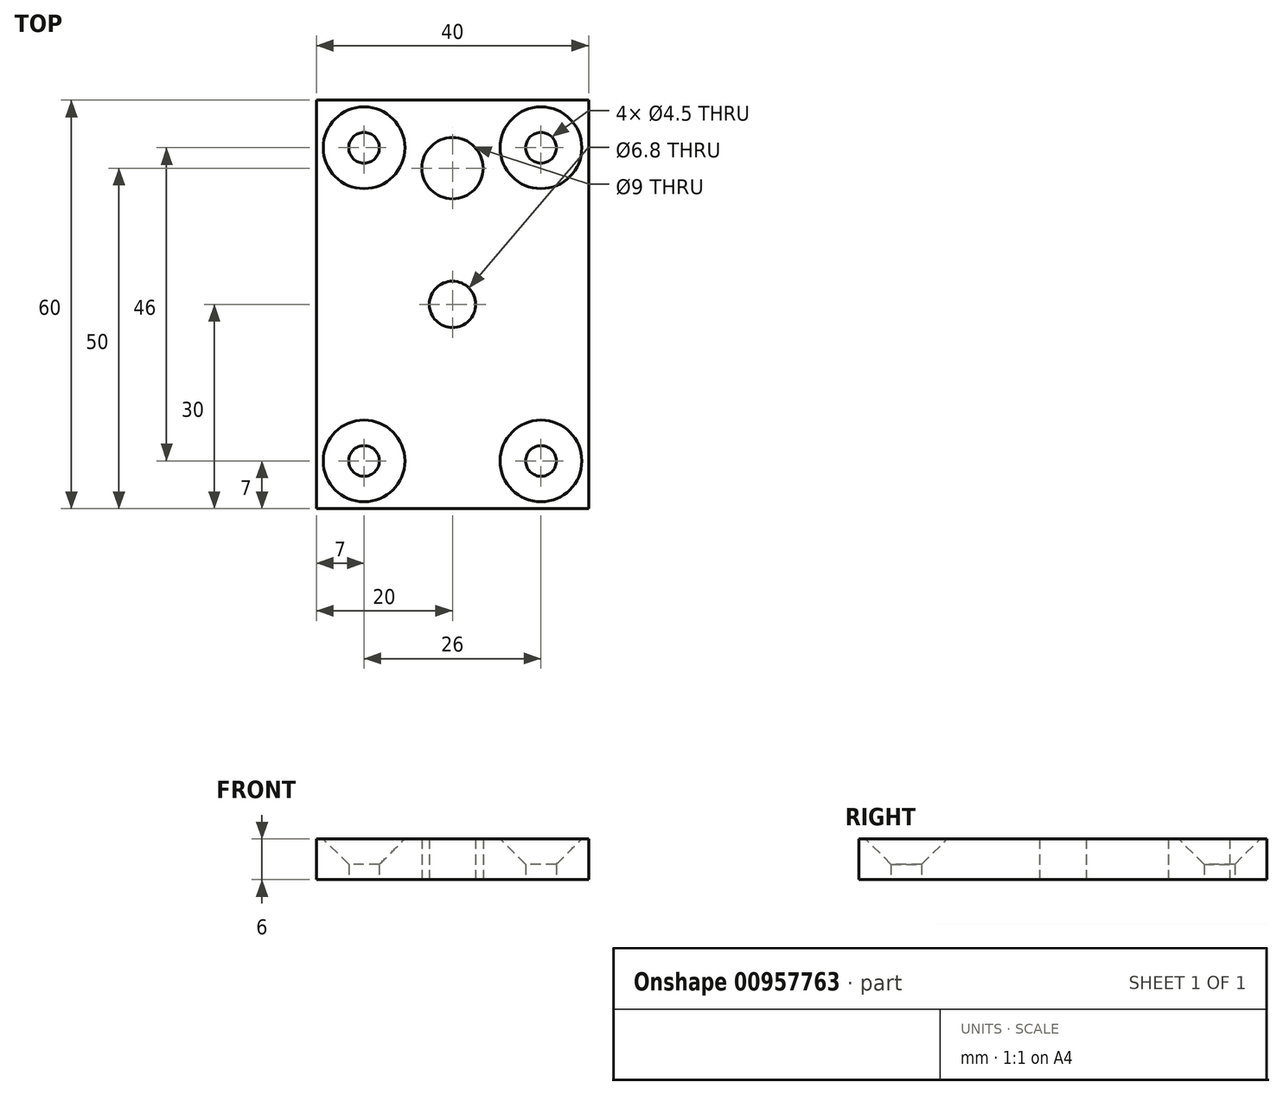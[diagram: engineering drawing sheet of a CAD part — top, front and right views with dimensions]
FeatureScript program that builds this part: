
annotation { "Feature Type Name" : "Feature", "Feature Type Description" : "" }
export const myFeature = defineFeature(function(context is Context, id is Id, definition is map)
    precondition{}
    {
        {
            var Q0;
            Q0=qCreatedBy(makeId("Top.planeOp"),FACE);
            var sketch = newSketch(context, id + "F0", { "sketchPlane" : qUnion([Q0])});
            skLineSegment(sketch, "E0.bottom", {"start": v(0, 0) * mm, "end": v(40, 0) * mm});
            skLineSegment(sketch, "E0.top", {"start": v(0, 60) * mm, "end": v(40, 60) * mm});
            skLineSegment(sketch, "E0.left", {"start": v(0, 0) * mm, "end": v(0, 60) * mm});
            skLineSegment(sketch, "E0.right", {"start": v(40, 0) * mm, "end": v(40, 60) * mm});
            skCircle(sketch, "E1", {"center": v(20, 50) * mm, "radius": 4.5 * mm});
            skCircle(sketch, "E2", {"center": v(20, 30) * mm, "radius": 3.4 * mm});
            skLineSegment(sketch, "E3", {"start": v(20, 68.34) * mm, "end": v(20, -17.74) * mm, "construction": true});
            skCircle(sketch, "E4", {"center": v(7, 53) * mm, "radius": 2.25 * mm});
            skCircle(sketch, "E5", {"center": v(33, 53) * mm, "radius": 2.25 * mm});
            skCircle(sketch, "E6", {"center": v(33, 7) * mm, "radius": 2.25 * mm});
            skCircle(sketch, "E7", {"center": v(7, 7) * mm, "radius": 2.25 * mm});
            skSolve(sketch);
        }
        {
            var Q0;
            Q0 = qSketchRegion(id + "F0", true);
            extrude(context, id + "F1", {"entities" : qUnion([Q0]), "depth" : 6 * mm, "offsetDistance" : 25 * mm});
        }
        {
            var Q0;
            Q0=makeQuery(id+"F1.opExtrude","CAP_EDGE",EDGE,{"disambiguationData":[OSD([sQuery(id+"F0.wireOp",EDGE,"E7")])],"isStart":false});
            var Q1;
            Q1=makeQuery(id+"F1.opExtrude","CAP_EDGE",EDGE,{"disambiguationData":[OSD([sQuery(id+"F0.wireOp",EDGE,"E6")])],"isStart":false});
            var Q2;
            Q2=makeQuery(id+"F1.opExtrude","CAP_EDGE",EDGE,{"disambiguationData":[OSD([sQuery(id+"F0.wireOp",EDGE,"E5")])],"isStart":false});
            var Q3;
            Q3=makeQuery(id+"F1.opExtrude","CAP_EDGE",EDGE,{"disambiguationData":[OSD([sQuery(id+"F0.wireOp",EDGE,"E4")])],"isStart":false});
            chamfer(context, id + "F2", {"entities" : qUnion([Q0, Q1, Q2, Q3]), "width" : 3.75 * mm, "tangentPropagation" : true});
        }
    });
